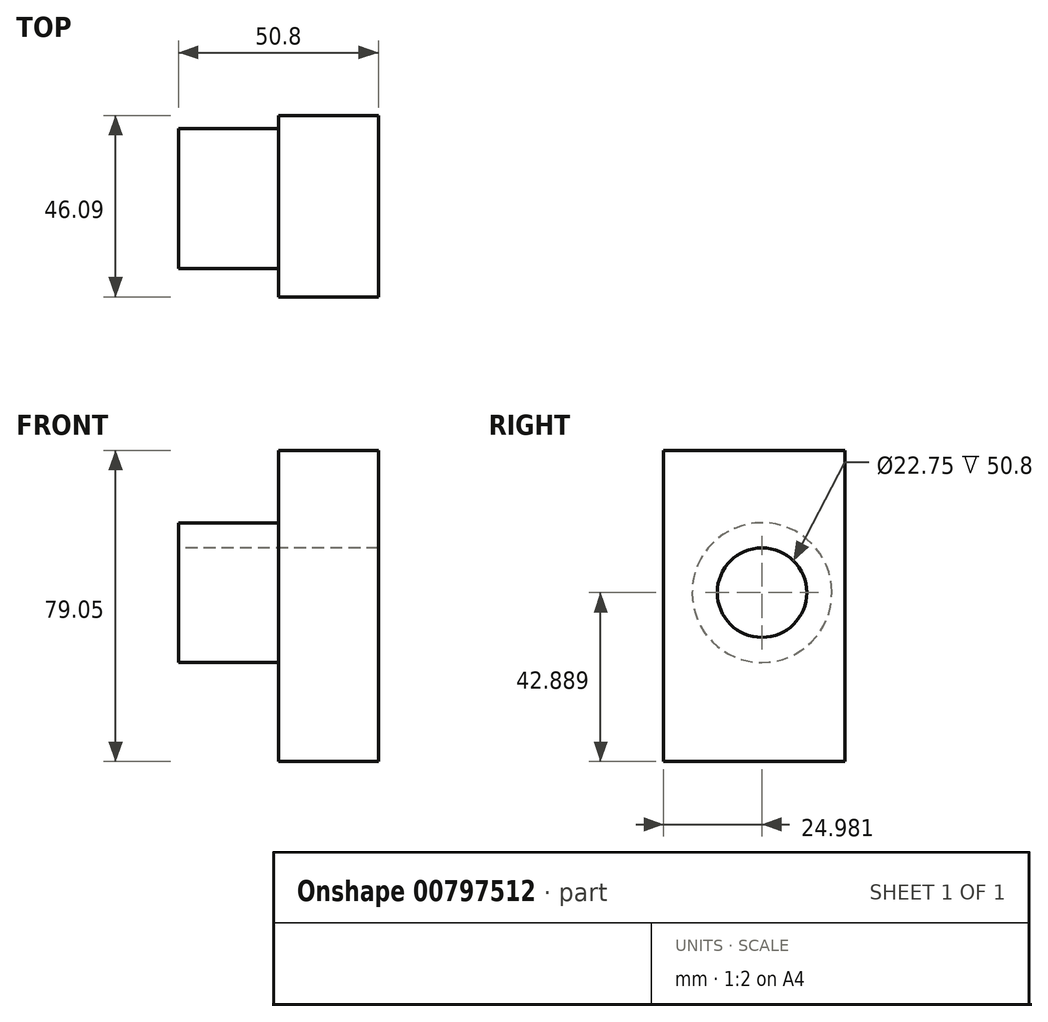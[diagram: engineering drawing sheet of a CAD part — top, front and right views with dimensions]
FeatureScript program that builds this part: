
annotation { "Feature Type Name" : "Feature", "Feature Type Description" : "" }
export const myFeature = defineFeature(function(context is Context, id is Id, definition is map)
    precondition{}
    {
        {
            var Q0;
            Q0=qCreatedBy(makeId("Right.planeOp"),FACE);
            var sketch = newSketch(context, id + "F0", { "sketchPlane" : qUnion([Q0])});
            skLineSegment(sketch, "E0.bottom", {"start": v(-19.54, 32.48) * mm, "end": v(26.55, 32.48) * mm});
            skLineSegment(sketch, "E0.top", {"start": v(-19.54, -46.57) * mm, "end": v(26.55, -46.57) * mm});
            skLineSegment(sketch, "E0.left", {"start": v(-19.54, 32.48) * mm, "end": v(-19.54, -46.57) * mm});
            skLineSegment(sketch, "E0.right", {"start": v(26.55, 32.48) * mm, "end": v(26.55, -46.57) * mm});
            skSolve(sketch);
        }
        {
            var Q0;
            Q0=makeQuery(id+"F0.imprint","IMPRINT",FACE,{"disambiguationData":[TD([[makeQuery(id+"F0.imprint","IMPRINT",EDGE,{"derivedFrom":sQuery(id+"F0.wireOp",EDGE,"E0.bottom")}),-1.0]])]});
            extrude(context, id + "F1", {"entities" : qUnion([Q0]), "depth" : 25.4 * mm, "offsetDistance" : 25.4 * mm});
        }
        {
            var Q0;
            Q0=makeQuery(id+"F1.opExtrude","CAP_FACE",FACE,{"disambiguationData":[OSD([sQuery(id+"F0.wireOp",EDGE,"E0.bottom"),sQuery(id+"F0.wireOp",EDGE,"E0.top"),sQuery(id+"F0.wireOp",EDGE,"E0.left"),sQuery(id+"F0.wireOp",EDGE,"E0.right")])],"isStart":true});
            var sketch = newSketch(context, id + "F2", { "sketchPlane" : qUnion([Q0])});
            skCircle(sketch, "E1", {"center": v(-5.44, -3.68) * mm, "radius": 17.75 * mm});
            skSolve(sketch);
        }
        {
            var Q0;
            Q0=makeQuery(id+"F2.imprint","IMPRINT",FACE,{"disambiguationData":[TD([[makeQuery(id+"F2.imprint","IMPRINT",EDGE,{"derivedFrom":sQuery(id+"F2.wireOp",EDGE,"E1")}),1.0]])]});
            extrude(context, id + "F3", {"entities" : qUnion([Q0]), "operationType" : NewBodyOperationType.ADD, "depth" : 25.4 * mm, "offsetDistance" : 25.4 * mm});
        }
        {
            var Q0;
            Q0=makeQuery(id+"F3.opExtrude","CAP_FACE",FACE,{"disambiguationData":[OSD([sQuery(id+"F2.wireOp",EDGE,"E1")])],"isStart":false});
            var sketch = newSketch(context, id + "F4", { "sketchPlane" : qUnion([Q0])});
            skCircle(sketch, "E2", {"center": v(-5.44, -3.68) * mm, "radius": 11.38 * mm});
            skSolve(sketch);
        }
        {
            var Q0;
            Q0=makeQuery(id+"F4.imprint","IMPRINT",FACE,{"disambiguationData":[TD([[makeQuery(id+"F4.imprint","IMPRINT",EDGE,{"derivedFrom":sQuery(id+"F4.wireOp",EDGE,"E2")}),1.0]])]});
            extrude(context, id + "F5", {"entities" : qUnion([Q0]), "operationType" : NewBodyOperationType.REMOVE, "endBound" : BoundingType.THROUGH_ALL, "oppositeDirection" : true, "depth" : 25.4 * mm, "offsetDistance" : 25.4 * mm});
        }
    });
